# Revit family: ADB Fourneaux Electrique L800IX
name_source: partatom
category: Equipement spécialisé
units: mm (PartAtom-declared; Revit-internal decimal feet)

## family parameters
Basée sur le plan de construction = Non
Conserver l'orientation des annotations = Non
Cote de connecteur circulaire = Utiliser le diamètre
Couper avec des vides une fois chargée = Non
Numéro OmniClass = 23.40.40.14.17.11
Partagée = Non
Repère de localisation dans la pièce = Non
Titre OmniClass = Cookers, Ovens, Stoves
Toujours verticalement = Oui
Type d'élément = Normal

## types (2) — shared parameters
B = 630 mm  [stored 2.06693 ft]
C = 290 mm  [stored 0.951444 ft]
Commentaires du type = Gamme Ambassade - Fourneaux électriques
Fabricant = Société Industrielle de Lacanche
URL = https://www.ambassade-de-bourgogne.com
zero-valued in all types: Elévation par défaut

## per-type parameters (varying)
| type | Description | Modèle | Panneau commande | Pbase | Poids net à vide | Table |
| 3 foyers induction 1 four Gastronorme - CE 831 IX | Fourneau électrique - 3 foyers induction 1 four électrique Gastronorme | CE 831 IX | CE831IX_Ecran Noir | 12400 W | 106.00 kg | CE831 IX_CE841 IX_3-4 foyers induction : CE 831 IX - 3 foyers |
| 4 foyers induction 1 four Gastronorme - CE 841 IX | Fourneau électrique - 4 foyers induction 1 four électrique Gastronorme | CE 841 IX | CE841IX_CE831IX_Ecran Tactile | 14800 W | 108.00 kg | CE831 IX_CE841 IX_3-4 foyers induction : CE 841 IX - 4 foyers |

note: [stored X ft] marks values corroborated as IEEE doubles in the binary element streams (Revit-internal decimal feet)
